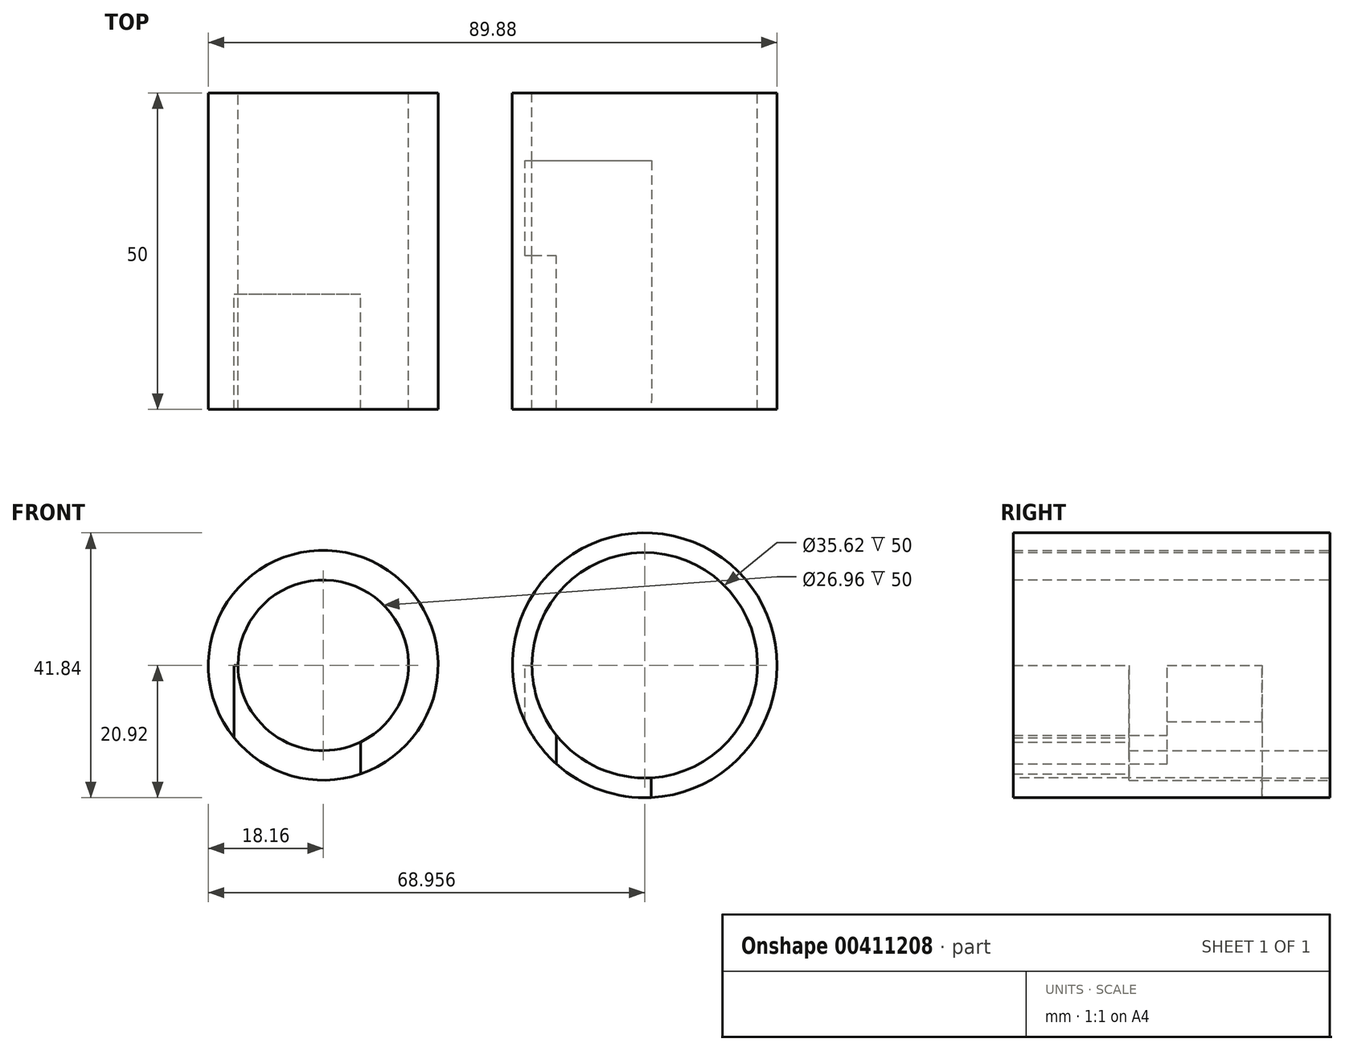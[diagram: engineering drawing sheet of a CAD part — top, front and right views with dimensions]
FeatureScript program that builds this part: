
annotation { "Feature Type Name" : "Feature", "Feature Type Description" : "" }
export const myFeature = defineFeature(function(context is Context, id is Id, definition is map)
    precondition{}
    {
        {
            var Q0;
            Q0=qCreatedBy(makeId("Front.planeOp"),FACE);
            var sketch = newSketch(context, id + "F0", { "sketchPlane" : qUnion([Q0])});
            skCircle(sketch, "E0", {"center": v(0, 0) * mm, "radius": 18.16 * mm});
            skCircle(sketch, "E1", {"center": v(0, 0) * mm, "radius": 13.48 * mm});
            skSolve(sketch);
        }
        {
            var Q0;
            Q0=makeQuery(id+"F0.imprint","IMPRINT",FACE,{"disambiguationData":[TD([[makeQuery(id+"F0.imprint","IMPRINT",EDGE,{"derivedFrom":sQuery(id+"F0.wireOp",EDGE,"E0")}),1.0]])]});
            extrude(context, id + "F1", {"entities" : qUnion([Q0]), "depth" : 50 * mm});
        }
        {
            var Q0;
            Q0=qCreatedBy(makeId("Top.planeOp"),FACE);
            var sketch = newSketch(context, id + "F2", { "sketchPlane" : qUnion([Q0])});
            skLineSegment(sketch, "E2", {"start": v(-14.1, -66.76) * mm, "end": v(-14.1, -31.76) * mm});
            skLineSegment(sketch, "E3", {"start": v(-14.1, -31.76) * mm, "end": v(5.9, -31.76) * mm});
            skLineSegment(sketch, "E4", {"start": v(5.9, -31.76) * mm, "end": v(5.9, -66.03) * mm});
            skLineSegment(sketch, "E5", {"start": v(5.9, -66.03) * mm, "end": v(-14.1, -66.76) * mm});
            skSolve(sketch);
        }
        {
            var Q0;
            Q0=makeQuery(id+"F2.imprint","IMPRINT",FACE,{"disambiguationData":[TD([[makeQuery(id+"F2.imprint","IMPRINT",EDGE,{"derivedFrom":sQuery(id+"F2.wireOp",EDGE,"E2")}),-1.0]])]});
            extrude(context, id + "F3", {"entities" : qUnion([Q0]), "operationType" : NewBodyOperationType.REMOVE, "oppositeDirection" : true, "depth" : 25 * mm});
        }
        {
            var Q0;
            Q0=qCreatedBy(makeId("Front.planeOp"),FACE);
            var sketch = newSketch(context, id + "F4", { "sketchPlane" : qUnion([Q0])});
            skCircle(sketch, "E6", {"center": v(50.8, 0) * mm, "radius": 20.92 * mm});
            skCircle(sketch, "E7", {"center": v(50.8, 0) * mm, "radius": 17.8 * mm});
            skSolve(sketch);
        }
        {
            var Q0;
            Q0=makeQuery(id+"F4.imprint","IMPRINT",FACE,{"disambiguationData":[TD([[makeQuery(id+"F4.imprint","IMPRINT",EDGE,{"derivedFrom":sQuery(id+"F4.wireOp",EDGE,"E6")}),1.0]])]});
            extrude(context, id + "F5", {"entities" : qUnion([Q0]), "depth" : 50 * mm});
        }
        {
            var Q0;
            Q0=qCreatedBy(makeId("Top.planeOp"),FACE);
            var sketch = newSketch(context, id + "F6", { "sketchPlane" : qUnion([Q0])});
            skLineSegment(sketch, "E8", {"start": v(51.85, -60.7) * mm, "end": v(36.85, -60.7) * mm});
            skLineSegment(sketch, "E9", {"start": v(36.85, -60.7) * mm, "end": v(36.85, -25.7) * mm});
            skLineSegment(sketch, "E10", {"start": v(36.85, -25.7) * mm, "end": v(31.87, -25.7) * mm});
            skLineSegment(sketch, "E11", {"start": v(31.87, -25.7) * mm, "end": v(31.87, -10.7) * mm});
            skLineSegment(sketch, "E12", {"start": v(31.87, -10.7) * mm, "end": v(51.87, -10.7) * mm});
            skLineSegment(sketch, "E13", {"start": v(51.87, -10.7) * mm, "end": v(51.85, -60.7) * mm});
            skSolve(sketch);
        }
        {
            var Q0;
            Q0=makeQuery(id+"F6.imprint","IMPRINT",FACE,{"disambiguationData":[TD([[makeQuery(id+"F6.imprint","IMPRINT",EDGE,{"derivedFrom":sQuery(id+"F6.wireOp",EDGE,"E8")}),-1.0]])]});
            extrude(context, id + "F7", {"entities" : qUnion([Q0]), "operationType" : NewBodyOperationType.REMOVE, "oppositeDirection" : true, "depth" : 25 * mm});
        }
    });
